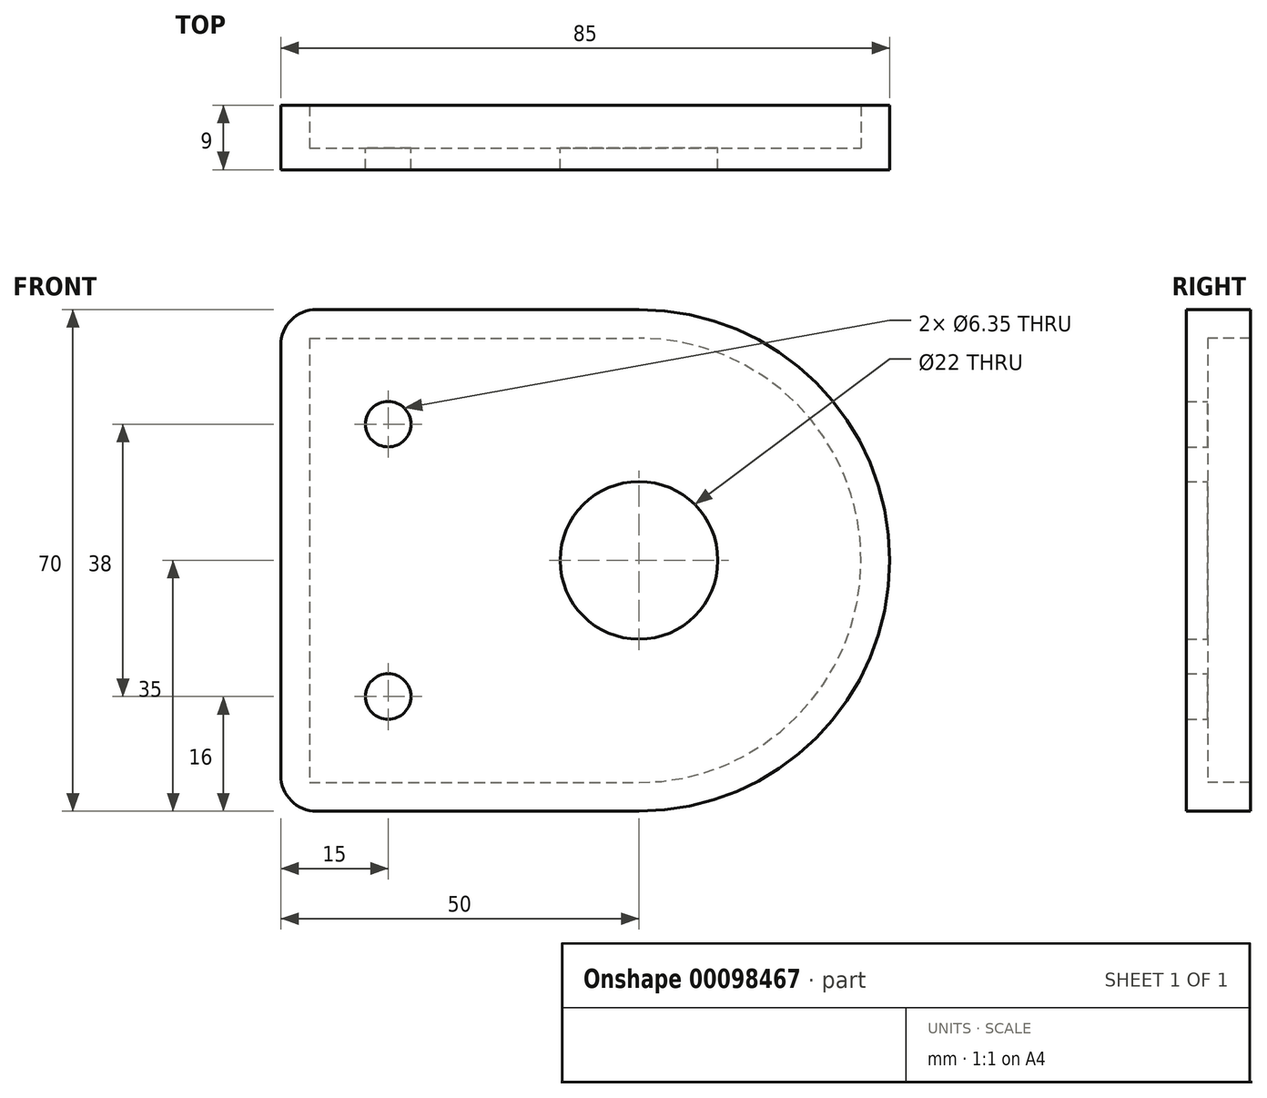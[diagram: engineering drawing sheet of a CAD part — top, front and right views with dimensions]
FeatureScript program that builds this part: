
annotation { "Feature Type Name" : "Feature", "Feature Type Description" : "" }
export const myFeature = defineFeature(function(context is Context, id is Id, definition is map)
    precondition{}
    {
        {
            var Q0;
            Q0=qCreatedBy(makeId("Front.planeOp"),FACE);
            var sketch = newSketch(context, id + "F0", { "sketchPlane" : qUnion([Q0])});
            skCircle(sketch, "E0", {"center": v(0, 19) * mm, "radius": 3.18 * mm});
            skCircle(sketch, "E1.MirrorC", {"center": v(0, -19) * mm, "radius": 3.18 * mm});
            skLineSegment(sketch, "E2", {"start": v(-15, 35) * mm, "end": v(35, 35) * mm});
            skCircle(sketch, "E3", {"center": v(35, 0) * mm, "radius": 11 * mm});
            skLineSegment(sketch, "E4.MirrorCS", {"start": v(16.96, -35) * mm, "end": v(16.96, 35) * mm, "construction": true});
            skLineSegment(sketch, "E5.MirrorCS", {"start": v(-15, -35) * mm, "end": v(35, -35) * mm});
            skLineSegment(sketch, "E6", {"start": v(-15, 35) * mm, "end": v(-15, -35) * mm});
            skLineSegment(sketch, "E7.bottom", {"start": v(50, -18.5) * mm, "end": v(20, -18.5) * mm, "construction": true});
            skLineSegment(sketch, "E7.top", {"start": v(50, 18.5) * mm, "end": v(20, 18.5) * mm, "construction": true});
            skLineSegment(sketch, "E7.left", {"start": v(50, -18.5) * mm, "end": v(50, 18.5) * mm, "construction": true});
            skLineSegment(sketch, "E7.right", {"start": v(20, -18.5) * mm, "end": v(20, 18.5) * mm, "construction": true});
            skCircle(sketch, "E8", {"center": v(35, 0) * mm, "radius": 35 * mm, "construction": true});
            skArc(sketch, "E9", {"start": v(35, 35) * mm, "mid": v(70, 0) * mm, "end": v(35, -35) * mm});
            skPoint(sketch, "E9.startSnap0", {"position": v(35, 18.5) * mm});
            skPoint(sketch, "E10.start.orphan", {"position": v(73, 35) * mm});
            skPoint(sketch, "E11.orphan", {"position": v(73, -35) * mm});
            skSolve(sketch);
        }
        {
            var Q0;
            Q0 = qSketchRegion(id + "F0", true);
            extrude(context, id + "F1", {"entities" : qUnion([Q0]), "depth" : 3 * mm});
        }
        {
            var Q0;
            Q0=makeQuery(id+"F1.opExtrude","SWEPT_BODY",BODY,{"disambiguationData":[OSD([sQuery(id+"F0.wireOp",EDGE,"E0"),sQuery(id+"F0.wireOp",EDGE,"E1.MirrorC"),sQuery(id+"F0.wireOp",EDGE,"E2"),sQuery(id+"F0.wireOp",EDGE,"E3"),sQuery(id+"F0.wireOp",EDGE,"E5.MirrorCS"),sQuery(id+"F0.wireOp",EDGE,"E10"),sQuery(id+"F0.wireOp",EDGE,"E6")])]});
            var Q1;
            Q1=qCreatedBy(makeId("Top.planeOp"),FACE);
            mirror(context, id + "F2", {"operationType" : NewBodyOperationType.ADD, "entities" : qUnion([Q0]), "mirrorPlane" : qUnion([Q1])});
        }
        {
            var Q0;
            Q0=makeQuery(id+"F1.opExtrude","SWEPT_EDGE",EDGE,{"disambiguationData":[OSD([sQuery(id+"F0.wireOp",EDGE,"E5.MirrorCS"),sQuery(id+"F0.wireOp",EDGE,"E6")])]});
            var Q1;
            Q1=makeQuery(id+"F1.opExtrude","SWEPT_EDGE",EDGE,{"disambiguationData":[OSD([sQuery(id+"F0.wireOp",EDGE,"E2"),sQuery(id+"F0.wireOp",EDGE,"E6")])]});
            var Q2;
            Q2=makeQuery(id+"F1.opExtrude","SWEPT_EDGE",EDGE,{"disambiguationData":[OSD([sQuery(id+"F0.wireOp",EDGE,"E2"),sQuery(id+"F0.wireOp",EDGE,"E10")])]});
            var Q3;
            Q3=makeQuery(id+"F1.opExtrude","SWEPT_EDGE",EDGE,{"disambiguationData":[OSD([sQuery(id+"F0.wireOp",EDGE,"E5.MirrorCS"),sQuery(id+"F0.wireOp",EDGE,"E10")])]});
            fillet(context, id + "F3", {"entities" : qUnion([Q0, Q1, Q2, Q3]), "radius" : 5 * mm, "tangentPropagation" : true, "allowEdgeOverflow" : false});
        }
        {
            var Q0;
            Q0=makeQuery(id+"F1.opExtrude","CAP_FACE",FACE,{"disambiguationData":[OSD([sQuery(id+"F0.wireOp",EDGE,"E0"),sQuery(id+"F0.wireOp",EDGE,"E1.MirrorC"),sQuery(id+"F0.wireOp",EDGE,"E2"),sQuery(id+"F0.wireOp",EDGE,"E3"),sQuery(id+"F0.wireOp",EDGE,"E5.MirrorCS"),sQuery(id+"F0.wireOp",EDGE,"E6"),sQuery(id+"F0.wireOp",EDGE,"E9")])],"isStart":true});
            var sketch = newSketch(context, id + "F4", { "sketchPlane" : qUnion([Q0])});
            skLineSegment(sketch, "E12.0", {"start": v(10, -35) * mm, "end": v(-35, -35) * mm});
            skArc(sketch, "E12.1", {"start": v(-35, 35) * mm, "mid": v(-70, 0) * mm, "end": v(-35, -35) * mm});
            skLineSegment(sketch, "E12.2", {"start": v(10, 35) * mm, "end": v(-35, 35) * mm});
            skLineSegment(sketch, "E12.3", {"start": v(15, 30) * mm, "end": v(15, -30) * mm});
            skArc(sketch, "E12.4", {"start": v(10, -35) * mm, "mid": v(13.54, -33.54) * mm, "end": v(15, -30) * mm});
            skArc(sketch, "E12.5", {"start": v(15, 30) * mm, "mid": v(13.54, 33.54) * mm, "end": v(10, 35) * mm});
            skLineSegment(sketch, "E13.0", {"start": v(11, 31) * mm, "end": v(11, -31) * mm});
            skLineSegment(sketch, "E13.1", {"start": v(11, 31) * mm, "end": v(-35, 31) * mm});
            skArc(sketch, "E13.2", {"start": v(-35, 31) * mm, "mid": v(-66, 0) * mm, "end": v(-35, -31) * mm});
            skLineSegment(sketch, "E13.3", {"start": v(11, -31) * mm, "end": v(-35, -31) * mm});
            skSolve(sketch);
        }
        {
            var Q0;
            Q0 = qSketchRegion(id + "F4", true);
            extrude(context, id + "F5", {"entities" : qUnion([Q0]), "operationType" : NewBodyOperationType.ADD, "depth" : 6 * mm});
        }
    });
